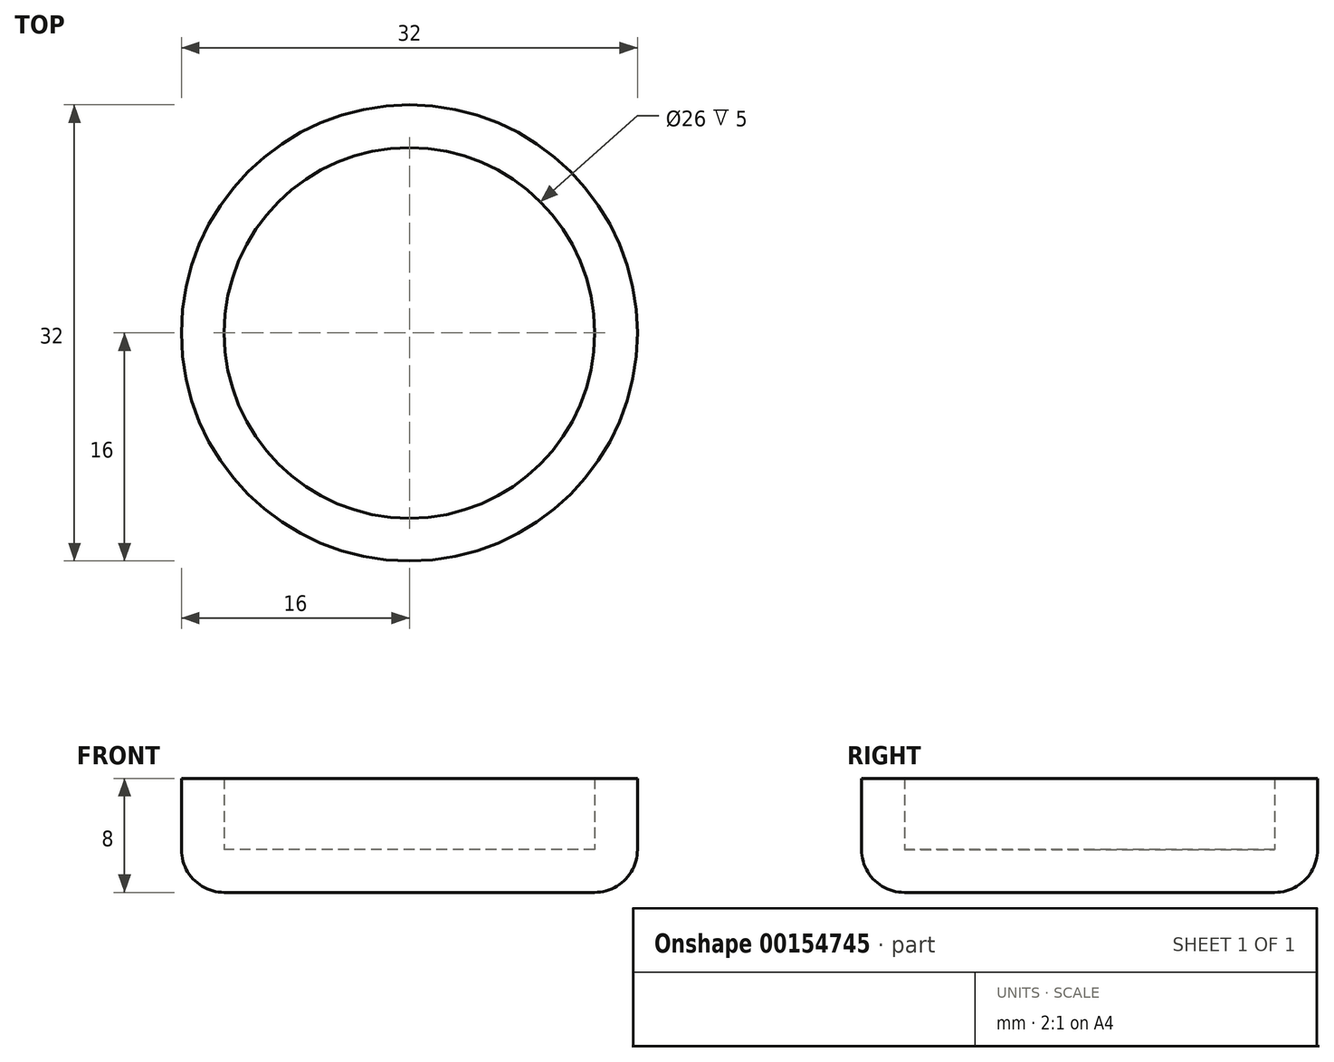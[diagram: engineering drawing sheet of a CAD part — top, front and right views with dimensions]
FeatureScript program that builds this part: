
annotation { "Feature Type Name" : "Feature", "Feature Type Description" : "" }
export const myFeature = defineFeature(function(context is Context, id is Id, definition is map)
    precondition{}
    {
        {
            var Q0;
            Q0=qCreatedBy(makeId("Top.planeOp"),FACE);
            var sketch = newSketch(context, id + "F0", { "sketchPlane" : qUnion([Q0])});
            skCircle(sketch, "E0", {"center": v(0, 0) * mm, "radius": 13 * mm});
            skCircle(sketch, "E1.0", {"center": v(0, 0) * mm, "radius": 16 * mm});
            skSolve(sketch);
        }
        {
            var Q0;
            Q0=makeQuery(id+"F0.imprint","IMPRINT",FACE,{"disambiguationData":[TD([[makeQuery(id+"F0.imprint","IMPRINT",EDGE,{"derivedFrom":sQuery(id+"F0.wireOp",EDGE,"E0")}),1.0]])]});
            extrude(context, id + "F1", {"entities" : qUnion([Q0]), "depth" : 3 * mm});
        }
        {
            var Q0;
            Q0 = qSketchRegion(id + "F0", true);
            extrude(context, id + "F2", {"entities" : qUnion([Q0]), "operationType" : NewBodyOperationType.ADD, "depth" : 8 * mm});
        }
        {
            var Q0;
            Q0=makeQuery(id+"F2.opExtrude","CAP_EDGE",EDGE,{"disambiguationData":[OSD([sQuery(id+"F0.wireOp",EDGE,"E1.0")])],"isStart":true});
            fillet(context, id + "F3", {"entities" : qUnion([Q0]), "radius" : 3 * mm, "tangentPropagation" : true, "allowEdgeOverflow" : false});
        }
    });
